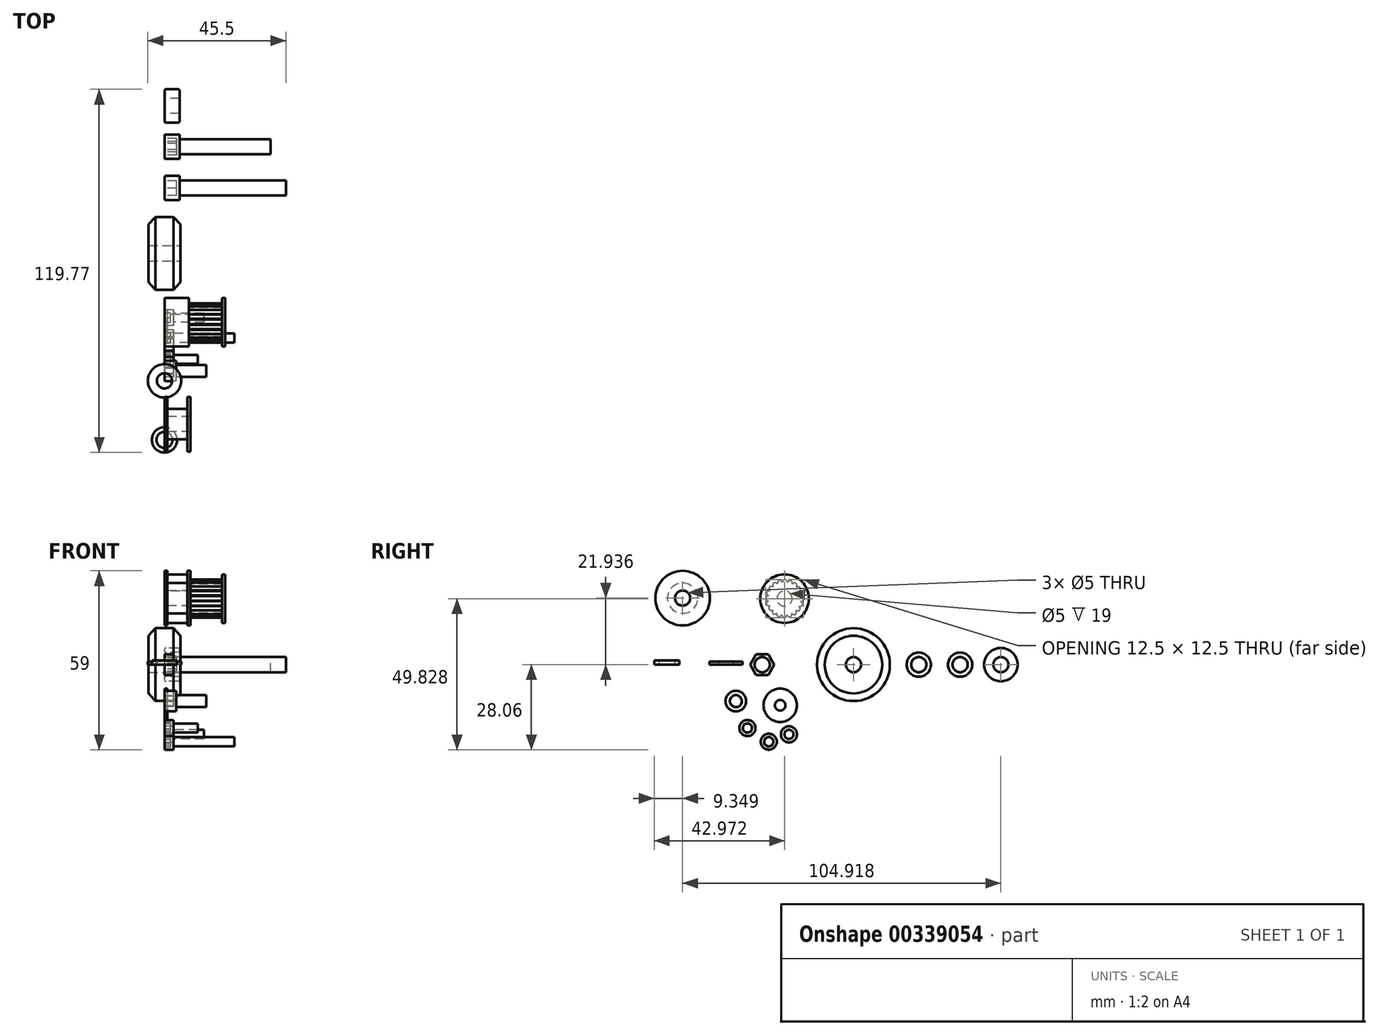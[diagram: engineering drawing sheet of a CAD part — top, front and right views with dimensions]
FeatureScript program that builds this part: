
annotation { "Feature Type Name" : "Feature", "Feature Type Description" : "" }
export const myFeature = defineFeature(function(context is Context, id is Id, definition is map)
    precondition{}
    {
        {
            var Q0;
            Q0=qCreatedBy(makeId("Top.planeOp"),FACE);
            var sketch = newSketch(context, id + "F0", { "sketchPlane" : qUnion([Q0])});
            skLineSegment(sketch, "E0", {"start": v(0, 12) * mm, "end": v(3, 12) * mm});
            skLineSegment(sketch, "E1", {"start": v(3, 12) * mm, "end": v(5.25, 9.5) * mm});
            skLineSegment(sketch, "E2", {"start": v(5.25, 9.5) * mm, "end": v(5.25, 2.5) * mm});
            skPoint(sketch, "E3.end.orphan", {"position": v(2.76, 0) * mm});
            skLineSegment(sketch, "E4", {"start": v(5.25, 2.5) * mm, "end": v(0, 2.5) * mm});
            skLineSegment(sketch, "E5", {"start": v(0, 2.5) * mm, "end": v(0, 12) * mm});
            skLineSegment(sketch, "E6.MirrorCS", {"start": v(0, 12) * mm, "end": v(-3, 12) * mm});
            skLineSegment(sketch, "E7.MirrorCS", {"start": v(-3, 12) * mm, "end": v(-5.25, 9.5) * mm});
            skLineSegment(sketch, "E8.MirrorCS", {"start": v(-5.25, 9.5) * mm, "end": v(-5.25, 2.5) * mm});
            skLineSegment(sketch, "E9.MirrorCS", {"start": v(-5.25, 2.5) * mm, "end": v(0, 2.5) * mm});
            skSolve(sketch);
        }
        {
            var Q0;
            Q0=qCreatedBy(makeId("Front.planeOp"),FACE);
            var sketch = newSketch(context, id + "F1", { "sketchPlane" : qUnion([Q0])});
            skLineSegment(sketch, "E10", {"start": v(9.9, 0) * mm, "end": v(-12.3, 0) * mm, "construction": true});
            skSolve(sketch);
        }
        {
            var Q0;
            Q0=qSketchRegion(id+"F0",true);
            var Q1;
            Q1=sQuery(id+"F1.wireOp",EDGE,"E10");
            revolve(context, id + "F2", {"entities" : qUnion([Q0]), "axis" : qUnion([Q1]), "revolveType" : RevolveType.FULL});
        }
        {
            var Q0;
            Q0=qCreatedBy(makeId("Right.planeOp"),FACE);
            var sketch = newSketch(context, id + "F3", { "sketchPlane" : qUnion([Q0])});
            skCircle(sketch, "E11", {"center": v(35.14, 0) * mm, "radius": 4 * mm});
            skSolve(sketch);
        }
        {
            var Q0;
            Q0=makeQuery(id+"F3.imprint","IMPRINT",FACE,{"disambiguationData":[TD([[makeQuery(id+"F3.imprint","IMPRINT",EDGE,{"derivedFrom":sQuery(id+"F3.wireOp",EDGE,"E11")}),1.0]])]});
            var Q1;
            Q1=sQuery(id+"F3.wireOp",EDGE,"E11");
            extrude(context, id + "F4", {"entities" : qUnion([Q0]), "surfaceEntities" : qUnion([Q1]), "depth" : 5 * mm});
        }
        {
            var Q0;
            Q0=makeQuery(id+"F4.opExtrude","CAP_FACE",FACE,{"disambiguationData":[OSD([sQuery(id+"F3.wireOp",EDGE,"E11")])],"isStart":false});
            var sketch = newSketch(context, id + "F5", { "sketchPlane" : qUnion([Q0])});
            skCircle(sketch, "E12", {"center": v(35.14, 0) * mm, "radius": 2.5 * mm});
            skSolve(sketch);
        }
        {
            var Q0;
            Q0=makeQuery(id+"F5.imprint","IMPRINT",FACE,{"disambiguationData":[TD([[makeQuery(id+"F5.imprint","IMPRINT",EDGE,{"derivedFrom":sQuery(id+"F5.wireOp",EDGE,"E12")}),1.0]])]});
            extrude(context, id + "F6", {"entities" : qUnion([Q0]), "operationType" : NewBodyOperationType.ADD, "depth" : 30 * mm});
        }
        {
            var Q0;
            Q0=makeQuery(id+"F4.opExtrude","CAP_FACE",FACE,{"disambiguationData":[OSD([sQuery(id+"F3.wireOp",EDGE,"E11")])],"isStart":true});
            var sketch = newSketch(context, id + "F7", { "sketchPlane" : qUnion([Q0])});
            skCircle(sketch, "E13.cCircle", {"center": v(-35.14, 0) * mm, "radius": 2.76 * mm, "construction": true});
            skLineSegment(sketch, "E13.0", {"start": v(-34.13, -2.56) * mm, "end": v(-36.86, -2.16) * mm});
            skLineSegment(sketch, "E13.1", {"start": v(-36.86, -2.16) * mm, "end": v(-37.87, 0.4) * mm});
            skLineSegment(sketch, "E13.2", {"start": v(-37.87, 0.4) * mm, "end": v(-36.16, 2.56) * mm});
            skLineSegment(sketch, "E13.3", {"start": v(-36.16, 2.56) * mm, "end": v(-33.43, 2.16) * mm});
            skLineSegment(sketch, "E13.4", {"start": v(-33.43, 2.16) * mm, "end": v(-32.42, -0.4) * mm});
            skLineSegment(sketch, "E13.5", {"start": v(-32.42, -0.4) * mm, "end": v(-34.13, -2.56) * mm});
            skSolve(sketch);
        }
        {
            var Q0;
            Q0=makeQuery(id+"F7.imprint","IMPRINT",FACE,{"disambiguationData":[TD([[makeQuery(id+"F7.imprint","IMPRINT",EDGE,{"derivedFrom":sQuery(id+"F7.wireOp",EDGE,"E13.0")}),-1.0]])]});
            extrude(context, id + "F8", {"entities" : qUnion([Q0]), "operationType" : NewBodyOperationType.REMOVE, "oppositeDirection" : true, "depth" : 4 * mm});
        }
        {
            var Q0;
            Q0=qCreatedBy(makeId("Right.planeOp"),FACE);
            var sketch = newSketch(context, id + "F9", { "sketchPlane" : qUnion([Q0])});
            skCircle(sketch, "E14", {"center": v(48.59, 0) * mm, "radius": 5.5 * mm});
            skCircle(sketch, "E15", {"center": v(48.59, 0) * mm, "radius": 2.5 * mm});
            skSolve(sketch);
        }
        {
            var Q0;
            Q0=qSketchRegion(id+"F9",true);
            extrude(context, id + "F10", {"entities" : qUnion([Q0]), "depth" : 5 * mm});
        }
        {
            var Q0;
            Q0=makeQuery(id+"F10.opExtrude","CAP_EDGE",EDGE,{"disambiguationData":[OSD([sQuery(id+"F9.wireOp",EDGE,"E14")])],"isStart":false});
            var Q1;
            Q1=makeQuery(id+"F10.opExtrude","CAP_EDGE",EDGE,{"disambiguationData":[OSD([sQuery(id+"F9.wireOp",EDGE,"E14")])],"isStart":true});
            fillet(context, id + "F11", {"entities" : qUnion([Q0, Q1]), "radius" : .5 * mm, "tangentPropagation" : true, "allowEdgeOverflow" : false});
        }
        {
            var Q0;
            Q0=qCreatedBy(makeId("Right.planeOp"),FACE);
            var sketch = newSketch(context, id + "F12", { "sketchPlane" : qUnion([Q0])});
            skCircle(sketch, "E16.cCircle", {"center": v(-30.1, 0) * mm, "radius": 4 * mm, "construction": true});
            skLineSegment(sketch, "E16.0", {"start": v(-28.07, -3.45) * mm, "end": v(-32.07, -3.48) * mm});
            skLineSegment(sketch, "E16.1", {"start": v(-32.07, -3.48) * mm, "end": v(-34.1, -0.04) * mm});
            skLineSegment(sketch, "E16.2", {"start": v(-34.1, -0.04) * mm, "end": v(-32.13, 3.45) * mm});
            skLineSegment(sketch, "E16.3", {"start": v(-32.13, 3.45) * mm, "end": v(-28.13, 3.48) * mm});
            skLineSegment(sketch, "E16.4", {"start": v(-28.13, 3.48) * mm, "end": v(-26.1, 0.04) * mm});
            skLineSegment(sketch, "E16.5", {"start": v(-26.1, 0.04) * mm, "end": v(-28.07, -3.45) * mm});
            skCircle(sketch, "E17", {"center": v(-30.1, 0) * mm, "radius": 2.5 * mm});
            skSolve(sketch);
        }
        {
            var Q0;
            Q0=makeQuery(id+"F12.imprint","IMPRINT",FACE,{"disambiguationData":[TD([[makeQuery(id+"F12.imprint","IMPRINT",EDGE,{"derivedFrom":sQuery(id+"F12.wireOp",EDGE,"E16.0")}),-1.0]])]});
            extrude(context, id + "F13", {"entities" : qUnion([Q0]), "depth" : 3 * mm});
        }
        {
            var Q0;
            Q0=qCreatedBy(makeId("Top.planeOp"),FACE);
            var sketch = newSketch(context, id + "F14", { "sketchPlane" : qUnion([Q0])});
            skCircle(sketch, "E18", {"center": v(0, -42.06) * mm, "radius": 5.5 * mm});
            skCircle(sketch, "E19", {"center": v(0, -42.06) * mm, "radius": 2.5 * mm});
            skSolve(sketch);
        }
        {
            var Q0;
            Q0=makeQuery(id+"F14.imprint","IMPRINT",FACE,{"disambiguationData":[TD([[makeQuery(id+"F14.imprint","IMPRINT",EDGE,{"derivedFrom":sQuery(id+"F14.wireOp",EDGE,"E18")}),1.0]])]});
            extrude(context, id + "F15", {"entities" : qUnion([Q0]), "depth" : 1 * mm});
        }
        {
            var Q0;
            Q0=qCreatedBy(makeId("Top.planeOp"),FACE);
            var sketch = newSketch(context, id + "F16", { "sketchPlane" : qUnion([Q0])});
            skCircle(sketch, "E20", {"center": v(0, -61.53) * mm, "radius": 4.15 * mm});
            skCircle(sketch, "E21", {"center": v(0, -61.53) * mm, "radius": 2.65 * mm});
            skSolve(sketch);
        }
        {
            var Q0;
            Q0=makeQuery(id+"F16.imprint","IMPRINT",FACE,{"disambiguationData":[TD([[makeQuery(id+"F16.imprint","IMPRINT",EDGE,{"derivedFrom":sQuery(id+"F16.wireOp",EDGE,"E20")}),1.0]])]});
            extrude(context, id + "F17", {"entities" : qUnion([Q0]), "depth" : 1.4 * mm});
        }
        {
            var Q0;
            Q0=qCreatedBy(makeId("Right.planeOp"),FACE);
            var sketch = newSketch(context, id + "F18", { "sketchPlane" : qUnion([Q0])});
            skCircle(sketch, "E22", {"center": v(-38.77, -12.03) * mm, "radius": 3.4 * mm});
            skSolve(sketch);
        }
        {
            var Q0;
            Q0=makeQuery(id+"F18.imprint","IMPRINT",FACE,{"disambiguationData":[TD([[makeQuery(id+"F18.imprint","IMPRINT",EDGE,{"derivedFrom":sQuery(id+"F18.wireOp",EDGE,"E22")}),1.0]])]});
            extrude(context, id + "F19", {"entities" : qUnion([Q0]), "depth" : 3.8 * mm});
        }
        {
            var Q0;
            Q0=makeQuery(id+"F19.opExtrude","CAP_FACE",FACE,{"disambiguationData":[OSD([sQuery(id+"F18.wireOp",EDGE,"E22")])],"isStart":true});
            fillet(context, id + "F20", {"entities" : qUnion([Q0]), "radius" : .5 * mm, "tangentPropagation" : true, "allowEdgeOverflow" : false});
        }
        {
            var Q0;
            Q0=makeQuery(id+"F19.opExtrude","CAP_FACE",FACE,{"disambiguationData":[OSD([sQuery(id+"F18.wireOp",EDGE,"E22")])],"isStart":true});
            var sketch = newSketch(context, id + "F21", { "sketchPlane" : qUnion([Q0])});
            skCircle(sketch, "E23.cCircle", {"center": v(38.77, -12.03) * mm, "radius": 1.7 * mm, "construction": true});
            skLineSegment(sketch, "E23.0", {"start": v(36.82, -11.85) * mm, "end": v(37.95, -10.25) * mm});
            skLineSegment(sketch, "E23.1", {"start": v(37.95, -10.25) * mm, "end": v(39.9, -10.42) * mm});
            skLineSegment(sketch, "E23.2", {"start": v(39.9, -10.42) * mm, "end": v(40.73, -12.2) * mm});
            skLineSegment(sketch, "E23.3", {"start": v(40.73, -12.2) * mm, "end": v(39.6, -13.8) * mm});
            skLineSegment(sketch, "E23.4", {"start": v(39.6, -13.8) * mm, "end": v(37.64, -13.63) * mm});
            skLineSegment(sketch, "E23.5", {"start": v(37.64, -13.63) * mm, "end": v(36.82, -11.85) * mm});
            skPoint(sketch, "E23.0.midPoint", {"position": v(37.38, -11.05) * mm});
            skSolve(sketch);
        }
        {
            var Q0;
            Q0=makeQuery(id+"F21.imprint","IMPRINT",FACE,{"disambiguationData":[TD([[makeQuery(id+"F21.imprint","IMPRINT",EDGE,{"derivedFrom":sQuery(id+"F21.wireOp",EDGE,"E23.0")}),-1.0]])]});
            extrude(context, id + "F22", {"entities" : qUnion([Q0]), "operationType" : NewBodyOperationType.REMOVE, "oppositeDirection" : true, "depth" : 3 * mm});
        }
        {
            var Q0;
            Q0=makeQuery(id+"F19.opExtrude","CAP_FACE",FACE,{"disambiguationData":[OSD([sQuery(id+"F18.wireOp",EDGE,"E22")])],"isStart":false});
            var sketch = newSketch(context, id + "F23", { "sketchPlane" : qUnion([Q0])});
            skCircle(sketch, "E24", {"center": v(-38.77, -12.03) * mm, "radius": 2 * mm});
            skSolve(sketch);
        }
        {
            var Q0;
            Q0=makeQuery(id+"F23.imprint","IMPRINT",FACE,{"disambiguationData":[TD([[makeQuery(id+"F23.imprint","IMPRINT",EDGE,{"derivedFrom":sQuery(id+"F23.wireOp",EDGE,"E24")}),1.0]])]});
            extrude(context, id + "F24", {"entities" : qUnion([Q0]), "operationType" : NewBodyOperationType.ADD, "depth" : 10 * mm});
        }
        {
            var Q0;
            Q0=qCreatedBy(makeId("Right.planeOp"),FACE);
            var sketch = newSketch(context, id + "F25", { "sketchPlane" : qUnion([Q0])});
            skCircle(sketch, "E25", {"center": v(-22.7, 21.77) * mm, "radius": 8 * mm});
            skSolve(sketch);
        }
        {
            var Q0;
            Q0=makeQuery(id+"F25.imprint","IMPRINT",FACE,{"disambiguationData":[TD([[makeQuery(id+"F25.imprint","IMPRINT",EDGE,{"derivedFrom":sQuery(id+"F25.wireOp",EDGE,"E25")}),1.0]])]});
            extrude(context, id + "F26", {"entities" : qUnion([Q0]), "depth" : 20 * mm});
        }
        {
            var Q0;
            Q0=makeQuery(id+"F26.opExtrude","CAP_FACE",FACE,{"disambiguationData":[OSD([sQuery(id+"F25.wireOp",EDGE,"E25")])],"isStart":false});
            cPlane(context, id + "F27", {"entities" : qUnion([Q0]), "cplaneType" : CPlaneType.OFFSET, "offset" : 1 * mm, "oppositeDirection" : true, "width" : 150 * mm, "height" : 150 * mm});
        }
        {
            var Q0;
            Q0=qCreatedBy(id+"F27.planeOp",FACE);
            var sketch = newSketch(context, id + "F28", { "sketchPlane" : qUnion([Q0])});
            skCircle(sketch, "E26", {"center": v(-22.7, 21.77) * mm, "radius": 8.85 * mm});
            skCircle(sketch, "E27", {"center": v(-22.7, 21.77) * mm, "radius": 5.5 * mm});
            skSolve(sketch);
        }
        {
            var Q0;
            Q0=makeQuery(id+"F28.imprint","IMPRINT",FACE,{"disambiguationData":[TD([[makeQuery(id+"F28.imprint","IMPRINT",EDGE,{"derivedFrom":sQuery(id+"F28.wireOp",EDGE,"E26")}),1.0]])]});
            extrude(context, id + "F29", {"entities" : qUnion([Q0]), "operationType" : NewBodyOperationType.REMOVE, "oppositeDirection" : true, "depth" : 11 * mm});
        }
        {
            var Q0;
            Q0=makeQuery(id+"F29.boolean.opBoolean","COPY",FACE,{"derivedFrom":makeQuery(id+"F29.opExtrude","CAP_FACE",FACE,{"disambiguationData":[OSD([sQuery(id+"F28.wireOp",EDGE,"E26"),sQuery(id+"F28.wireOp",EDGE,"E27")])],"isStart":false})});
            var sketch = newSketch(context, id + "F30", { "sketchPlane" : qUnion([Q0])});
            skCircle(sketch, "E28", {"center": v(-28.2, 21.86) * mm, "radius": 0.75 * mm});
            skCircle(sketch, "E29.1.0", {"center": v(-27.97, 20.16) * mm, "radius": 0.75 * mm});
            skCircle(sketch, "E29.2.0", {"center": v(-27.21, 18.61) * mm, "radius": 0.75 * mm});
            skCircle(sketch, "E29.3.0", {"center": v(-26.02, 17.38) * mm, "radius": 0.75 * mm});
            skCircle(sketch, "E29.4.0", {"center": v(-24.5, 16.57) * mm, "radius": 0.75 * mm});
            skCircle(sketch, "E29.5.0", {"center": v(-22.8, 16.27) * mm, "radius": 0.75 * mm});
            skCircle(sketch, "E29.6.0", {"center": v(-21.1, 16.5) * mm, "radius": 0.75 * mm});
            skCircle(sketch, "E29.7.0", {"center": v(-19.55, 17.26) * mm, "radius": 0.75 * mm});
            skCircle(sketch, "E29.8.0", {"center": v(-18.32, 18.46) * mm, "radius": 0.75 * mm});
            skCircle(sketch, "E29.9.0", {"center": v(-17.5, 19.98) * mm, "radius": 0.75 * mm});
            skCircle(sketch, "E29.10.0", {"center": v(-17.2, 21.67) * mm, "radius": 0.75 * mm});
            skCircle(sketch, "E29.11.0", {"center": v(-17.45, 23.38) * mm, "radius": 0.75 * mm});
            skCircle(sketch, "E29.12.0", {"center": v(-18.2, 24.92) * mm, "radius": 0.75 * mm});
            skCircle(sketch, "E29.13.0", {"center": v(-19.4, 26.16) * mm, "radius": 0.75 * mm});
            skCircle(sketch, "E29.14.0", {"center": v(-20.92, 26.97) * mm, "radius": 0.75 * mm});
            skCircle(sketch, "E29.15.0", {"center": v(-22.61, 27.27) * mm, "radius": 0.75 * mm});
            skPoint(sketch, "E29.center", {"position": v(-22.7, 21.77) * mm});
            skCircle(sketch, "E30.1.16.0", {"center": v(-24.32, 27.03) * mm, "radius": 0.75 * mm});
            skCircle(sketch, "E30.1.17.0", {"center": v(-25.86, 26.27) * mm, "radius": 0.75 * mm});
            skCircle(sketch, "E30.1.18.0", {"center": v(-27.1, 25.08) * mm, "radius": 0.75 * mm});
            skCircle(sketch, "E30.1.19.0", {"center": v(-27.9, 23.56) * mm, "radius": 0.75 * mm});
            skSolve(sketch);
        }
        {
            var Q0;
            {var subQ0=sQuery(id+"F30.wireOp",EDGE,"E28");var subQ1=makeQuery(id+"F29.boolean.opBoolean","COPY",EDGE,{"derivedFrom":makeQuery(id+"F29.opExtrude","CAP_EDGE",EDGE,{"disambiguationData":[OSD([sQuery(id+"F28.wireOp",EDGE,"E27")])],"isStart":false})});var subQ2=makeQuery(id+"F30.imprint","INTERSECT",VERTEX,{"disambiguationData":[OD(0.0)],"derivedFrom":[subQ1,subQ0]});Q0=makeQuery(id+"F30.imprint","IMPRINT",FACE,{"disambiguationData":[TD([[makeQuery(id+"F30.imprint","IMPRINT",EDGE,{"disambiguationData":[TD([[subQ2,1.0]])],"derivedFrom":subQ0}),1.0]])]});}
            var Q1;
            {var subQ0=sQuery(id+"F30.wireOp",EDGE,"E30.1.19.0");var subQ1=makeQuery(id+"F29.boolean.opBoolean","COPY",EDGE,{"derivedFrom":makeQuery(id+"F29.opExtrude","CAP_EDGE",EDGE,{"disambiguationData":[OSD([sQuery(id+"F28.wireOp",EDGE,"E27")])],"isStart":false})});var subQ2=makeQuery(id+"F30.imprint","INTERSECT",VERTEX,{"disambiguationData":[OD(0.0)],"derivedFrom":[subQ1,subQ0]});Q1=makeQuery(id+"F30.imprint","IMPRINT",FACE,{"disambiguationData":[TD([[makeQuery(id+"F30.imprint","IMPRINT",EDGE,{"disambiguationData":[TD([[subQ2,1.0]])],"derivedFrom":subQ0}),1.0]])]});}
            var Q2;
            {var subQ0=sQuery(id+"F30.wireOp",EDGE,"E30.1.18.0");var subQ1=makeQuery(id+"F29.boolean.opBoolean","COPY",EDGE,{"derivedFrom":makeQuery(id+"F29.opExtrude","CAP_EDGE",EDGE,{"disambiguationData":[OSD([sQuery(id+"F28.wireOp",EDGE,"E27")])],"isStart":false})});var subQ2=makeQuery(id+"F30.imprint","INTERSECT",VERTEX,{"disambiguationData":[OD(0.0)],"derivedFrom":[subQ1,subQ0]});Q2=makeQuery(id+"F30.imprint","IMPRINT",FACE,{"disambiguationData":[TD([[makeQuery(id+"F30.imprint","IMPRINT",EDGE,{"disambiguationData":[TD([[subQ2,1.0]])],"derivedFrom":subQ0}),1.0]])]});}
            var Q3;
            {var subQ0=sQuery(id+"F30.wireOp",EDGE,"E30.1.17.0");var subQ1=makeQuery(id+"F29.boolean.opBoolean","COPY",EDGE,{"derivedFrom":makeQuery(id+"F29.opExtrude","CAP_EDGE",EDGE,{"disambiguationData":[OSD([sQuery(id+"F28.wireOp",EDGE,"E27")])],"isStart":false})});var subQ2=makeQuery(id+"F30.imprint","INTERSECT",VERTEX,{"disambiguationData":[OD(0.0)],"derivedFrom":[subQ1,subQ0]});Q3=makeQuery(id+"F30.imprint","IMPRINT",FACE,{"disambiguationData":[TD([[makeQuery(id+"F30.imprint","IMPRINT",EDGE,{"disambiguationData":[TD([[subQ2,1.0]])],"derivedFrom":subQ0}),1.0]])]});}
            var Q4;
            {var subQ0=sQuery(id+"F30.wireOp",EDGE,"E30.1.16.0");var subQ1=makeQuery(id+"F29.boolean.opBoolean","COPY",EDGE,{"derivedFrom":makeQuery(id+"F29.opExtrude","CAP_EDGE",EDGE,{"disambiguationData":[OSD([sQuery(id+"F28.wireOp",EDGE,"E27")])],"isStart":false})});var subQ2=makeQuery(id+"F30.imprint","INTERSECT",VERTEX,{"disambiguationData":[OD(0.0)],"derivedFrom":[subQ1,subQ0]});Q4=makeQuery(id+"F30.imprint","IMPRINT",FACE,{"disambiguationData":[TD([[makeQuery(id+"F30.imprint","IMPRINT",EDGE,{"disambiguationData":[TD([[subQ2,1.0]])],"derivedFrom":subQ0}),1.0]])]});}
            var Q5;
            {var subQ0=sQuery(id+"F30.wireOp",EDGE,"E29.15.0");var subQ1=makeQuery(id+"F29.boolean.opBoolean","COPY",EDGE,{"derivedFrom":makeQuery(id+"F29.opExtrude","CAP_EDGE",EDGE,{"disambiguationData":[OSD([sQuery(id+"F28.wireOp",EDGE,"E27")])],"isStart":false})});var subQ2=makeQuery(id+"F30.imprint","INTERSECT",VERTEX,{"disambiguationData":[OD(0.0)],"derivedFrom":[subQ1,subQ0]});Q5=makeQuery(id+"F30.imprint","IMPRINT",FACE,{"disambiguationData":[TD([[makeQuery(id+"F30.imprint","IMPRINT",EDGE,{"disambiguationData":[TD([[subQ2,1.0]])],"derivedFrom":subQ0}),1.0]])]});}
            var Q6;
            {var subQ0=sQuery(id+"F30.wireOp",EDGE,"E29.14.0");var subQ1=makeQuery(id+"F29.boolean.opBoolean","COPY",EDGE,{"derivedFrom":makeQuery(id+"F29.opExtrude","CAP_EDGE",EDGE,{"disambiguationData":[OSD([sQuery(id+"F28.wireOp",EDGE,"E27")])],"isStart":false})});var subQ2=makeQuery(id+"F30.imprint","INTERSECT",VERTEX,{"disambiguationData":[OD(0.0)],"derivedFrom":[subQ1,subQ0]});Q6=makeQuery(id+"F30.imprint","IMPRINT",FACE,{"disambiguationData":[TD([[makeQuery(id+"F30.imprint","IMPRINT",EDGE,{"disambiguationData":[TD([[subQ2,1.0]])],"derivedFrom":subQ0}),1.0]])]});}
            var Q7;
            {var subQ0=sQuery(id+"F30.wireOp",EDGE,"E29.1.0");var subQ1=makeQuery(id+"F29.boolean.opBoolean","COPY",EDGE,{"derivedFrom":makeQuery(id+"F29.opExtrude","CAP_EDGE",EDGE,{"disambiguationData":[OSD([sQuery(id+"F28.wireOp",EDGE,"E27")])],"isStart":false})});var subQ2=makeQuery(id+"F30.imprint","INTERSECT",VERTEX,{"disambiguationData":[OD(0.0)],"derivedFrom":[subQ1,subQ0]});Q7=makeQuery(id+"F30.imprint","IMPRINT",FACE,{"disambiguationData":[TD([[makeQuery(id+"F30.imprint","IMPRINT",EDGE,{"disambiguationData":[TD([[subQ2,1.0]])],"derivedFrom":subQ0}),1.0]])]});}
            var Q8;
            {var subQ0=sQuery(id+"F30.wireOp",EDGE,"E29.2.0");var subQ1=makeQuery(id+"F29.boolean.opBoolean","COPY",EDGE,{"derivedFrom":makeQuery(id+"F29.opExtrude","CAP_EDGE",EDGE,{"disambiguationData":[OSD([sQuery(id+"F28.wireOp",EDGE,"E27")])],"isStart":false})});var subQ2=makeQuery(id+"F30.imprint","INTERSECT",VERTEX,{"disambiguationData":[OD(0.0)],"derivedFrom":[subQ1,subQ0]});Q8=makeQuery(id+"F30.imprint","IMPRINT",FACE,{"disambiguationData":[TD([[makeQuery(id+"F30.imprint","IMPRINT",EDGE,{"disambiguationData":[TD([[subQ2,-1.0]])],"derivedFrom":subQ0}),1.0]])]});}
            var Q9;
            {var subQ0=sQuery(id+"F30.wireOp",EDGE,"E29.3.0");var subQ1=makeQuery(id+"F29.boolean.opBoolean","COPY",EDGE,{"derivedFrom":makeQuery(id+"F29.opExtrude","CAP_EDGE",EDGE,{"disambiguationData":[OSD([sQuery(id+"F28.wireOp",EDGE,"E27")])],"isStart":false})});var subQ2=makeQuery(id+"F30.imprint","INTERSECT",VERTEX,{"disambiguationData":[OD(0.0)],"derivedFrom":[subQ1,subQ0]});Q9=makeQuery(id+"F30.imprint","IMPRINT",FACE,{"disambiguationData":[TD([[makeQuery(id+"F30.imprint","IMPRINT",EDGE,{"disambiguationData":[TD([[subQ2,-1.0]])],"derivedFrom":subQ0}),1.0]])]});}
            var Q10;
            {var subQ0=sQuery(id+"F30.wireOp",EDGE,"E29.4.0");var subQ1=makeQuery(id+"F29.boolean.opBoolean","COPY",EDGE,{"derivedFrom":makeQuery(id+"F29.opExtrude","CAP_EDGE",EDGE,{"disambiguationData":[OSD([sQuery(id+"F28.wireOp",EDGE,"E27")])],"isStart":false})});var subQ2=makeQuery(id+"F30.imprint","INTERSECT",VERTEX,{"disambiguationData":[OD(0.0)],"derivedFrom":[subQ1,subQ0]});Q10=makeQuery(id+"F30.imprint","IMPRINT",FACE,{"disambiguationData":[TD([[makeQuery(id+"F30.imprint","IMPRINT",EDGE,{"disambiguationData":[TD([[subQ2,-1.0]])],"derivedFrom":subQ0}),1.0]])]});}
            var Q11;
            {var subQ0=sQuery(id+"F30.wireOp",EDGE,"E29.5.0");var subQ1=makeQuery(id+"F29.boolean.opBoolean","COPY",EDGE,{"derivedFrom":makeQuery(id+"F29.opExtrude","CAP_EDGE",EDGE,{"disambiguationData":[OSD([sQuery(id+"F28.wireOp",EDGE,"E27")])],"isStart":false})});var subQ2=makeQuery(id+"F30.imprint","INTERSECT",VERTEX,{"disambiguationData":[OD(0.0)],"derivedFrom":[subQ1,subQ0]});Q11=makeQuery(id+"F30.imprint","IMPRINT",FACE,{"disambiguationData":[TD([[makeQuery(id+"F30.imprint","IMPRINT",EDGE,{"disambiguationData":[TD([[subQ2,-1.0]])],"derivedFrom":subQ0}),1.0]])]});}
            var Q12;
            {var subQ0=sQuery(id+"F30.wireOp",EDGE,"E29.7.0");var subQ1=makeQuery(id+"F29.boolean.opBoolean","COPY",EDGE,{"derivedFrom":makeQuery(id+"F29.opExtrude","CAP_EDGE",EDGE,{"disambiguationData":[OSD([sQuery(id+"F28.wireOp",EDGE,"E27")])],"isStart":false})});var subQ2=makeQuery(id+"F30.imprint","INTERSECT",VERTEX,{"disambiguationData":[OD(0.0)],"derivedFrom":[subQ1,subQ0]});Q12=makeQuery(id+"F30.imprint","IMPRINT",FACE,{"disambiguationData":[TD([[makeQuery(id+"F30.imprint","IMPRINT",EDGE,{"disambiguationData":[TD([[subQ2,-1.0]])],"derivedFrom":subQ0}),1.0]])]});}
            var Q13;
            {var subQ0=sQuery(id+"F30.wireOp",EDGE,"E29.6.0");var subQ1=makeQuery(id+"F29.boolean.opBoolean","COPY",EDGE,{"derivedFrom":makeQuery(id+"F29.opExtrude","CAP_EDGE",EDGE,{"disambiguationData":[OSD([sQuery(id+"F28.wireOp",EDGE,"E27")])],"isStart":false})});var subQ2=makeQuery(id+"F30.imprint","INTERSECT",VERTEX,{"disambiguationData":[OD(0.0)],"derivedFrom":[subQ1,subQ0]});Q13=makeQuery(id+"F30.imprint","IMPRINT",FACE,{"disambiguationData":[TD([[makeQuery(id+"F30.imprint","IMPRINT",EDGE,{"disambiguationData":[TD([[subQ2,-1.0]])],"derivedFrom":subQ0}),1.0]])]});}
            var Q14;
            {var subQ0=sQuery(id+"F30.wireOp",EDGE,"E29.8.0");var subQ1=makeQuery(id+"F29.boolean.opBoolean","COPY",EDGE,{"derivedFrom":makeQuery(id+"F29.opExtrude","CAP_EDGE",EDGE,{"disambiguationData":[OSD([sQuery(id+"F28.wireOp",EDGE,"E27")])],"isStart":false})});var subQ2=makeQuery(id+"F30.imprint","INTERSECT",VERTEX,{"disambiguationData":[OD(0.0)],"derivedFrom":[subQ1,subQ0]});Q14=makeQuery(id+"F30.imprint","IMPRINT",FACE,{"disambiguationData":[TD([[makeQuery(id+"F30.imprint","IMPRINT",EDGE,{"disambiguationData":[TD([[subQ2,-1.0]])],"derivedFrom":subQ0}),1.0]])]});}
            var Q15;
            {var subQ0=sQuery(id+"F30.wireOp",EDGE,"E29.9.0");var subQ1=makeQuery(id+"F29.boolean.opBoolean","COPY",EDGE,{"derivedFrom":makeQuery(id+"F29.opExtrude","CAP_EDGE",EDGE,{"disambiguationData":[OSD([sQuery(id+"F28.wireOp",EDGE,"E27")])],"isStart":false})});var subQ2=makeQuery(id+"F30.imprint","INTERSECT",VERTEX,{"disambiguationData":[OD(0.0)],"derivedFrom":[subQ1,subQ0]});Q15=makeQuery(id+"F30.imprint","IMPRINT",FACE,{"disambiguationData":[TD([[makeQuery(id+"F30.imprint","IMPRINT",EDGE,{"disambiguationData":[TD([[subQ2,-1.0]])],"derivedFrom":subQ0}),1.0]])]});}
            var Q16;
            {var subQ0=sQuery(id+"F30.wireOp",EDGE,"E29.10.0");var subQ1=makeQuery(id+"F29.boolean.opBoolean","COPY",EDGE,{"derivedFrom":makeQuery(id+"F29.opExtrude","CAP_EDGE",EDGE,{"disambiguationData":[OSD([sQuery(id+"F28.wireOp",EDGE,"E27")])],"isStart":false})});var subQ2=makeQuery(id+"F30.imprint","INTERSECT",VERTEX,{"disambiguationData":[OD(0.0)],"derivedFrom":[subQ1,subQ0]});Q16=makeQuery(id+"F30.imprint","IMPRINT",FACE,{"disambiguationData":[TD([[makeQuery(id+"F30.imprint","IMPRINT",EDGE,{"disambiguationData":[TD([[subQ2,-1.0]])],"derivedFrom":subQ0}),1.0]])]});}
            var Q17;
            {var subQ0=sQuery(id+"F30.wireOp",EDGE,"E29.11.0");var subQ1=makeQuery(id+"F29.boolean.opBoolean","COPY",EDGE,{"derivedFrom":makeQuery(id+"F29.opExtrude","CAP_EDGE",EDGE,{"disambiguationData":[OSD([sQuery(id+"F28.wireOp",EDGE,"E27")])],"isStart":false})});var subQ2=makeQuery(id+"F30.imprint","INTERSECT",VERTEX,{"disambiguationData":[OD(0.0)],"derivedFrom":[subQ1,subQ0]});Q17=makeQuery(id+"F30.imprint","IMPRINT",FACE,{"disambiguationData":[TD([[makeQuery(id+"F30.imprint","IMPRINT",EDGE,{"disambiguationData":[TD([[subQ2,-1.0]])],"derivedFrom":subQ0}),1.0]])]});}
            var Q18;
            {var subQ0=sQuery(id+"F30.wireOp",EDGE,"E29.12.0");var subQ1=makeQuery(id+"F29.boolean.opBoolean","COPY",EDGE,{"derivedFrom":makeQuery(id+"F29.opExtrude","CAP_EDGE",EDGE,{"disambiguationData":[OSD([sQuery(id+"F28.wireOp",EDGE,"E27")])],"isStart":false})});var subQ2=makeQuery(id+"F30.imprint","INTERSECT",VERTEX,{"disambiguationData":[OD(0.0)],"derivedFrom":[subQ1,subQ0]});Q18=makeQuery(id+"F30.imprint","IMPRINT",FACE,{"disambiguationData":[TD([[makeQuery(id+"F30.imprint","IMPRINT",EDGE,{"disambiguationData":[TD([[subQ2,1.0]])],"derivedFrom":subQ0}),1.0]])]});}
            var Q19;
            {var subQ0=sQuery(id+"F30.wireOp",EDGE,"E29.13.0");var subQ1=makeQuery(id+"F29.boolean.opBoolean","COPY",EDGE,{"derivedFrom":makeQuery(id+"F29.opExtrude","CAP_EDGE",EDGE,{"disambiguationData":[OSD([sQuery(id+"F28.wireOp",EDGE,"E27")])],"isStart":false})});var subQ2=makeQuery(id+"F30.imprint","INTERSECT",VERTEX,{"disambiguationData":[OD(0.0)],"derivedFrom":[subQ1,subQ0]});Q19=makeQuery(id+"F30.imprint","IMPRINT",FACE,{"disambiguationData":[TD([[makeQuery(id+"F30.imprint","IMPRINT",EDGE,{"disambiguationData":[TD([[subQ2,1.0]])],"derivedFrom":subQ0}),1.0]])]});}
            var Q20;
            Q20=sQuery(id+"F30.wireOp",EDGE,"E28");
            extrude(context, id + "F31", {"entities" : qUnion([Q0, Q1, Q2, Q3, Q4, Q5, Q6, Q7, Q8, Q9, Q10, Q11, Q12, Q13, Q14, Q15, Q16, Q17, Q18, Q19]), "operationType" : NewBodyOperationType.ADD, "surfaceEntities" : qUnion([Q20]), "endBound" : BoundingType.UP_TO_NEXT, "depth" : 25 * mm});
        }
        {
            var Q0;
            Q0=makeQuery(id+"F26.opExtrude","CAP_FACE",FACE,{"disambiguationData":[OSD([sQuery(id+"F25.wireOp",EDGE,"E25")])],"isStart":true});
            var sketch = newSketch(context, id + "F32", { "sketchPlane" : qUnion([Q0])});
            skCircle(sketch, "E31", {"center": v(22.7, 21.77) * mm, "radius": 2.5 * mm});
            skSolve(sketch);
        }
        {
            var Q0;
            Q0=makeQuery(id+"F32.imprint","IMPRINT",FACE,{"disambiguationData":[TD([[makeQuery(id+"F32.imprint","IMPRINT",EDGE,{"derivedFrom":sQuery(id+"F32.wireOp",EDGE,"E31")}),1.0]])]});
            extrude(context, id + "F33", {"entities" : qUnion([Q0]), "operationType" : NewBodyOperationType.REMOVE, "oppositeDirection" : true, "depth" : 19 * mm});
        }
        {
            var Q0;
            Q0=qCreatedBy(makeId("Right.planeOp"),FACE);
            var sketch = newSketch(context, id + "F34", { "sketchPlane" : qUnion([Q0])});
            skCircle(sketch, "E32", {"center": v(21.52, 0) * mm, "radius": 4 * mm});
            skSolve(sketch);
        }
        {
            var Q0;
            Q0=qSketchRegion(id+"F34",true);
            extrude(context, id + "F35", {"entities" : qUnion([Q0]), "depth" : 5 * mm});
        }
        {
            var Q0;
            Q0=makeQuery(id+"F35.opExtrude","CAP_FACE",FACE,{"disambiguationData":[OSD([sQuery(id+"F34.wireOp",EDGE,"E32")])],"isStart":false});
            var sketch = newSketch(context, id + "F36", { "sketchPlane" : qUnion([Q0])});
            skCircle(sketch, "E33", {"center": v(21.52, 0) * mm, "radius": 2.5 * mm});
            skSolve(sketch);
        }
        {
            var Q0;
            Q0=makeQuery(id+"F36.imprint","IMPRINT",FACE,{"disambiguationData":[TD([[makeQuery(id+"F36.imprint","IMPRINT",EDGE,{"derivedFrom":sQuery(id+"F36.wireOp",EDGE,"E33")}),1.0]])]});
            extrude(context, id + "F37", {"entities" : qUnion([Q0]), "operationType" : NewBodyOperationType.ADD, "depth" : 35 * mm});
        }
        {
            var Q0;
            Q0=makeQuery(id+"F35.opExtrude","CAP_EDGE",EDGE,{"disambiguationData":[OSD([sQuery(id+"F34.wireOp",EDGE,"E32")])],"isStart":true});
            fillet(context, id + "F38", {"entities" : qUnion([Q0]), "radius" : .5 * mm, "tangentPropagation" : true, "allowEdgeOverflow" : false});
        }
        {
            var Q0;
            Q0=makeQuery(id+"F35.opExtrude","CAP_FACE",FACE,{"disambiguationData":[OSD([sQuery(id+"F34.wireOp",EDGE,"E32")])],"isStart":true});
            var sketch = newSketch(context, id + "F39", { "sketchPlane" : qUnion([Q0])});
            skCircle(sketch, "E34.cCircle", {"center": v(-21.52, 0) * mm, "radius": 2.41 * mm, "construction": true});
            skLineSegment(sketch, "E34.0", {"start": v(-23.94, -1.4) * mm, "end": v(-23.94, 1.4) * mm});
            skLineSegment(sketch, "E34.1", {"start": v(-23.94, 1.4) * mm, "end": v(-21.52, 2.79) * mm});
            skLineSegment(sketch, "E34.2", {"start": v(-21.52, 2.79) * mm, "end": v(-19.11, 1.4) * mm});
            skLineSegment(sketch, "E34.3", {"start": v(-19.11, 1.4) * mm, "end": v(-19.11, -1.4) * mm});
            skLineSegment(sketch, "E34.4", {"start": v(-19.11, -1.4) * mm, "end": v(-21.52, -2.79) * mm});
            skLineSegment(sketch, "E34.5", {"start": v(-21.52, -2.79) * mm, "end": v(-23.94, -1.4) * mm});
            skPoint(sketch, "E34.0.midPoint", {"position": v(-23.94, 0) * mm});
            skSolve(sketch);
        }
        {
            var Q0;
            Q0=makeQuery(id+"F39.imprint","IMPRINT",FACE,{"disambiguationData":[TD([[makeQuery(id+"F39.imprint","IMPRINT",EDGE,{"derivedFrom":sQuery(id+"F39.wireOp",EDGE,"E34.0")}),-1.0]])]});
            extrude(context, id + "F40", {"entities" : qUnion([Q0]), "operationType" : NewBodyOperationType.REMOVE, "oppositeDirection" : true, "depth" : 4 * mm});
        }
        {
            var Q0;
            Q0=qCreatedBy(makeId("Right.planeOp"),FACE);
            var sketch = newSketch(context, id + "F41", { "sketchPlane" : qUnion([Q0])});
            skCircle(sketch, "E35", {"center": v(-56.33, 21.94) * mm, "radius": 9 * mm});
            skCircle(sketch, "E36", {"center": v(-56.33, 21.94) * mm, "radius": 2.5 * mm});
            skSolve(sketch);
        }
        {
            var Q0;
            Q0=makeQuery(id+"F41.imprint","IMPRINT",FACE,{"disambiguationData":[TD([[makeQuery(id+"F41.imprint","IMPRINT",EDGE,{"derivedFrom":sQuery(id+"F41.wireOp",EDGE,"E35")}),1.0]])]});
            extrude(context, id + "F42", {"entities" : qUnion([Q0]), "depth" : 8.6 * mm});
        }
        {
            var Q0;
            Q0=makeQuery(id+"F42.opExtrude","CAP_FACE",FACE,{"disambiguationData":[OSD([sQuery(id+"F41.wireOp",EDGE,"E35"),sQuery(id+"F41.wireOp",EDGE,"E36")])],"isStart":false});
            cPlane(context, id + "F43", {"entities" : qUnion([Q0]), "cplaneType" : CPlaneType.OFFSET, "offset" : 1 * mm, "oppositeDirection" : true, "width" : 150 * mm, "height" : 150 * mm});
        }
        {
            var Q0;
            Q0=qCreatedBy(id+"F43.planeOp",FACE);
            var sketch = newSketch(context, id + "F44", { "sketchPlane" : qUnion([Q0])});
            skCircle(sketch, "E37", {"center": v(-56.33, 21.94) * mm, "radius": 5 * mm});
            skCircle(sketch, "E38", {"center": v(-56.33, 21.94) * mm, "radius": 10.26 * mm});
            skSolve(sketch);
        }
        {
            var Q0;
            Q0=makeQuery(id+"F44.imprint","IMPRINT",FACE,{"disambiguationData":[TD([[makeQuery(id+"F44.imprint","IMPRINT",EDGE,{"derivedFrom":sQuery(id+"F44.wireOp",EDGE,"E37")}),-1.0]])]});
            extrude(context, id + "F45", {"entities" : qUnion([Q0]), "operationType" : NewBodyOperationType.REMOVE, "oppositeDirection" : true, "depth" : 6.6 * mm});
        }
        {
            var Q0;
            Q0=qCreatedBy(makeId("Right.planeOp"),FACE);
            var sketch = newSketch(context, id + "F46", { "sketchPlane" : qUnion([Q0])});
            skCircle(sketch, "E39", {"center": v(-21.28, -22.98) * mm, "radius": 2.65 * mm});
            skSolve(sketch);
        }
        {
            var Q0;
            Q0=makeQuery(id+"F46.imprint","IMPRINT",FACE,{"disambiguationData":[TD([[makeQuery(id+"F46.imprint","IMPRINT",EDGE,{"derivedFrom":sQuery(id+"F46.wireOp",EDGE,"E39")}),1.0]])]});
            var Q1;
            Q1=sQuery(id+"F46.wireOp",EDGE,"E39");
            extrude(context, id + "F47", {"entities" : qUnion([Q0]), "surfaceEntities" : qUnion([Q1]), "depth" : 3 * mm});
        }
        {
            var Q0;
            Q0=makeQuery(id+"F47.opExtrude","CAP_FACE",FACE,{"disambiguationData":[OSD([sQuery(id+"F46.wireOp",EDGE,"E39")])],"isStart":false});
            var sketch = newSketch(context, id + "F48", { "sketchPlane" : qUnion([Q0])});
            skCircle(sketch, "E40", {"center": v(-21.28, -22.98) * mm, "radius": 1.5 * mm});
            skSolve(sketch);
        }
        {
            var Q0;
            Q0=makeQuery(id+"F48.imprint","IMPRINT",FACE,{"disambiguationData":[TD([[makeQuery(id+"F48.imprint","IMPRINT",EDGE,{"derivedFrom":sQuery(id+"F48.wireOp",EDGE,"E40")}),1.0]])]});
            extrude(context, id + "F49", {"entities" : qUnion([Q0]), "operationType" : NewBodyOperationType.ADD, "depth" : 10 * mm});
        }
        {
            var Q0;
            Q0=makeQuery(id+"F47.opExtrude","CAP_FACE",FACE,{"disambiguationData":[OSD([sQuery(id+"F46.wireOp",EDGE,"E39")])],"isStart":true});
            var sketch = newSketch(context, id + "F50", { "sketchPlane" : qUnion([Q0])});
            skCircle(sketch, "E41.cCircle", {"center": v(21.28, -22.98) * mm, "radius": 1.55 * mm, "construction": true});
            skLineSegment(sketch, "E41.0", {"start": v(19.73, -23.88) * mm, "end": v(19.73, -22.1) * mm});
            skLineSegment(sketch, "E41.1", {"start": v(19.73, -22.1) * mm, "end": v(21.28, -21.2) * mm});
            skLineSegment(sketch, "E41.2", {"start": v(21.28, -21.2) * mm, "end": v(22.82, -22.1) * mm});
            skLineSegment(sketch, "E41.3", {"start": v(22.82, -22.1) * mm, "end": v(22.82, -23.88) * mm});
            skLineSegment(sketch, "E41.4", {"start": v(22.82, -23.88) * mm, "end": v(21.28, -24.77) * mm});
            skLineSegment(sketch, "E41.5", {"start": v(21.28, -24.77) * mm, "end": v(19.73, -23.88) * mm});
            skPoint(sketch, "E41.0.midPoint", {"position": v(19.73, -22.98) * mm});
            skSolve(sketch);
        }
        {
            var Q0;
            Q0=makeQuery(id+"F50.imprint","IMPRINT",FACE,{"disambiguationData":[TD([[makeQuery(id+"F50.imprint","IMPRINT",EDGE,{"derivedFrom":sQuery(id+"F50.wireOp",EDGE,"E41.0")}),-1.0]])]});
            extrude(context, id + "F51", {"entities" : qUnion([Q0]), "operationType" : NewBodyOperationType.REMOVE, "oppositeDirection" : true, "depth" : 2 * mm});
        }
        {
            var Q0;
            Q0=qCreatedBy(makeId("Right.planeOp"),FACE);
            var sketch = newSketch(context, id + "F52", { "sketchPlane" : qUnion([Q0])});
            skCircle(sketch, "E42", {"center": v(-34.96, -20.91) * mm, "radius": 2.65 * mm});
            skSolve(sketch);
        }
        {
            var Q0;
            Q0=makeQuery(id+"F52.imprint","IMPRINT",FACE,{"disambiguationData":[TD([[makeQuery(id+"F52.imprint","IMPRINT",EDGE,{"derivedFrom":sQuery(id+"F52.wireOp",EDGE,"E42")}),1.0]])]});
            var Q1;
            Q1=sQuery(id+"F52.wireOp",EDGE,"E42");
            extrude(context, id + "F53", {"entities" : qUnion([Q0]), "surfaceEntities" : qUnion([Q1]), "depth" : 3 * mm});
        }
        {
            var Q0;
            Q0=makeQuery(id+"F53.opExtrude","CAP_FACE",FACE,{"disambiguationData":[OSD([sQuery(id+"F52.wireOp",EDGE,"E42")])],"isStart":false});
            var sketch = newSketch(context, id + "F54", { "sketchPlane" : qUnion([Q0])});
            skCircle(sketch, "E43", {"center": v(-34.96, -20.91) * mm, "radius": 1.5 * mm});
            skSolve(sketch);
        }
        {
            var Q0;
            Q0=makeQuery(id+"F54.imprint","IMPRINT",FACE,{"disambiguationData":[TD([[makeQuery(id+"F54.imprint","IMPRINT",EDGE,{"derivedFrom":sQuery(id+"F54.wireOp",EDGE,"E43")}),1.0]])]});
            extrude(context, id + "F55", {"entities" : qUnion([Q0]), "operationType" : NewBodyOperationType.ADD, "depth" : 8 * mm});
        }
        {
            var Q0;
            Q0=makeQuery(id+"F53.opExtrude","CAP_FACE",FACE,{"disambiguationData":[OSD([sQuery(id+"F52.wireOp",EDGE,"E42")])],"isStart":true});
            var sketch = newSketch(context, id + "F56", { "sketchPlane" : qUnion([Q0])});
            skCircle(sketch, "E44.cCircle", {"center": v(34.96, -20.91) * mm, "radius": 1.68 * mm, "construction": true});
            skLineSegment(sketch, "E44.0", {"start": v(33.1, -20.36) * mm, "end": v(34.5, -19.03) * mm});
            skLineSegment(sketch, "E44.1", {"start": v(34.5, -19.03) * mm, "end": v(36.36, -19.58) * mm});
            skLineSegment(sketch, "E44.2", {"start": v(36.36, -19.58) * mm, "end": v(36.82, -21.46) * mm});
            skLineSegment(sketch, "E44.3", {"start": v(36.82, -21.46) * mm, "end": v(35.4, -22.8) * mm});
            skLineSegment(sketch, "E44.4", {"start": v(35.4, -22.8) * mm, "end": v(33.55, -22.24) * mm});
            skLineSegment(sketch, "E44.5", {"start": v(33.55, -22.24) * mm, "end": v(33.1, -20.36) * mm});
            skPoint(sketch, "E44.0.midPoint", {"position": v(33.8, -19.7) * mm});
            skSolve(sketch);
        }
        {
            var Q0;
            Q0=makeQuery(id+"F56.imprint","IMPRINT",FACE,{"disambiguationData":[TD([[makeQuery(id+"F56.imprint","IMPRINT",EDGE,{"derivedFrom":sQuery(id+"F56.wireOp",EDGE,"E44.0")}),-1.0]])]});
            extrude(context, id + "F57", {"entities" : qUnion([Q0]), "operationType" : NewBodyOperationType.REMOVE, "oppositeDirection" : true, "depth" : 2 * mm});
        }
        {
            var Q0;
            Q0=qCreatedBy(makeId("Right.planeOp"),FACE);
            var sketch = newSketch(context, id + "F58", { "sketchPlane" : qUnion([Q0])});
            skCircle(sketch, "E45", {"center": v(-27.92, -25.4) * mm, "radius": 2.65 * mm});
            skSolve(sketch);
        }
        {
            var Q0;
            Q0=makeQuery(id+"F58.imprint","IMPRINT",FACE,{"disambiguationData":[TD([[makeQuery(id+"F58.imprint","IMPRINT",EDGE,{"derivedFrom":sQuery(id+"F58.wireOp",EDGE,"E45")}),1.0]])]});
            extrude(context, id + "F59", {"entities" : qUnion([Q0]), "depth" : 3 * mm});
        }
        {
            var Q0;
            Q0=makeQuery(id+"F59.opExtrude","CAP_FACE",FACE,{"disambiguationData":[OSD([sQuery(id+"F58.wireOp",EDGE,"E45")])],"isStart":false});
            var sketch = newSketch(context, id + "F60", { "sketchPlane" : qUnion([Q0])});
            skCircle(sketch, "E46", {"center": v(-27.92, -25.4) * mm, "radius": 1.5 * mm});
            skSolve(sketch);
        }
        {
            var Q0;
            Q0=makeQuery(id+"F60.imprint","IMPRINT",FACE,{"disambiguationData":[TD([[makeQuery(id+"F60.imprint","IMPRINT",EDGE,{"derivedFrom":sQuery(id+"F60.wireOp",EDGE,"E46")}),1.0]])]});
            extrude(context, id + "F61", {"entities" : qUnion([Q0]), "operationType" : NewBodyOperationType.ADD, "depth" : 20 * mm});
        }
        {
            var Q0;
            Q0=makeQuery(id+"F59.opExtrude","CAP_FACE",FACE,{"disambiguationData":[OSD([sQuery(id+"F58.wireOp",EDGE,"E45")])],"isStart":true});
            var sketch = newSketch(context, id + "F62", { "sketchPlane" : qUnion([Q0])});
            skCircle(sketch, "E47.cCircle", {"center": v(27.92, -25.4) * mm, "radius": 1.68 * mm, "construction": true});
            skLineSegment(sketch, "E47.0", {"start": v(27.6, -23.5) * mm, "end": v(29.41, -24.17) * mm});
            skLineSegment(sketch, "E47.1", {"start": v(29.41, -24.17) * mm, "end": v(29.74, -26.08) * mm});
            skLineSegment(sketch, "E47.2", {"start": v(29.74, -26.08) * mm, "end": v(28.25, -27.32) * mm});
            skLineSegment(sketch, "E47.3", {"start": v(28.25, -27.32) * mm, "end": v(26.43, -26.65) * mm});
            skLineSegment(sketch, "E47.4", {"start": v(26.43, -26.65) * mm, "end": v(26.1, -24.74) * mm});
            skLineSegment(sketch, "E47.5", {"start": v(26.1, -24.74) * mm, "end": v(27.6, -23.5) * mm});
            skPoint(sketch, "E47.0.midPoint", {"position": v(28.5, -23.83) * mm});
            skSolve(sketch);
        }
        {
            var Q0;
            Q0=makeQuery(id+"F62.imprint","IMPRINT",FACE,{"disambiguationData":[TD([[makeQuery(id+"F62.imprint","IMPRINT",EDGE,{"derivedFrom":sQuery(id+"F62.wireOp",EDGE,"E47.0")}),-1.0]])]});
            extrude(context, id + "F63", {"entities" : qUnion([Q0]), "operationType" : NewBodyOperationType.REMOVE, "oppositeDirection" : true, "depth" : 2 * mm});
        }
        {
            var Q0;
            Q0=qCreatedBy(makeId("Right.planeOp"),FACE);
            var sketch = newSketch(context, id + "F64", { "sketchPlane" : qUnion([Q0])});
            skCircle(sketch, "E48", {"center": v(-24.16, -13.4) * mm, "radius": 5.5 * mm});
            skCircle(sketch, "E49", {"center": v(-24.16, -13.4) * mm, "radius": 1.75 * mm});
            skSolve(sketch);
        }
        {
            var Q0;
            Q0=makeQuery(id+"F64.imprint","IMPRINT",FACE,{"disambiguationData":[TD([[makeQuery(id+"F64.imprint","IMPRINT",EDGE,{"derivedFrom":sQuery(id+"F64.wireOp",EDGE,"E48")}),1.0]])]});
            extrude(context, id + "F65", {"entities" : qUnion([Q0]), "depth" : 1 * mm});
        }
        {
            var Q0;
            Q0=makeQuery(id+"F65.opExtrude","CAP_EDGE",EDGE,{"disambiguationData":[OSD([sQuery(id+"F64.wireOp",EDGE,"E48")])],"isStart":false});
            var Q1;
            Q1=makeQuery(id+"F65.opExtrude","CAP_EDGE",EDGE,{"disambiguationData":[OSD([sQuery(id+"F64.wireOp",EDGE,"E49")])],"isStart":false});
            var Q2;
            Q2=makeQuery(id+"F65.opExtrude","CAP_EDGE",EDGE,{"disambiguationData":[OSD([sQuery(id+"F64.wireOp",EDGE,"E49")])],"isStart":true});
            var Q3;
            Q3=makeQuery(id+"F65.opExtrude","CAP_EDGE",EDGE,{"disambiguationData":[OSD([sQuery(id+"F64.wireOp",EDGE,"E48")])],"isStart":true});
            fillet(context, id + "F66", {"entities" : qUnion([Q0, Q1, Q2, Q3]), "radius" : .3 * mm, "tangentPropagation" : true, "allowEdgeOverflow" : false});
        }
    });
